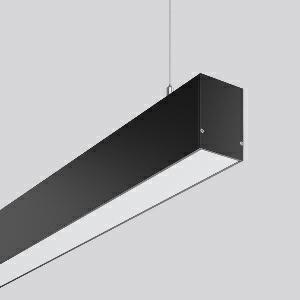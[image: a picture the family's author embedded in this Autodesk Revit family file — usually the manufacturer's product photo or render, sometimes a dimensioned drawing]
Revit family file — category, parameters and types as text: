
# Revit family: less_is_more_50_312313_003_1_1fba
name_source: partatom
category: Lighting Fixtures
units: mm (PartAtom-declared; Revit-internal decimal feet)

## family parameters
Cut with Voids When Loaded = No
Host = Face
Light Source = No
Part Type = Normal
Room Calculation Point = No
Round Connector Dimension = Use Diameter
Shared = No

## types (1)
- LESS IS MORE 50 (1 x LED Modul 840, 4050 lm, 4000)
    Apparent Load = 34 VA
    CIE Flux Codes = 48 79 95 100 100
    Color Rendering = 80
    Color Temperature = 4000
    Default Elevation = 1800 mm
    Description = Series: LESS IS MORE 50
Linear pendant luminaire for aesthetically sophisticated lighting. Housing: extruded aluminium profile, powder-coated. End cap aluminium powder-coated. Canopy made of aluminium, powder-coated. Diffuser made of non-yellowing plastic (PMMA), opal. Direct light emission. Suitable for pendant. 2-point steel cable suspension freely positionable and infinitely height-adjustable. Special lengths available on request. LED unit with integrated converter interchangeable and removable. Suitable for through-wiring. With sensors or as a safety luminaire on request. 
Colour: deep black, matt (RAL 9005)
Length: 1407 mm
Width: 57 mm
Height: 75 mm
Suspension length: 2000 mm
Lamp: LED
Socket: without socket
Colour temperature: 4000K
Colour rendering index (CRI): 80
System power: 34 W
Rated luminous flux: 4050 lm
Luminous efficiency: 119 lm/W
Control gear: Regulated power supply
Protection class: I
Type of protection: IP 20
    Height = 75 mm
    Lamp = 1 x LED Modul 840
    Lamp Light Flux = 4050 lm
    Lamp count = 1
    Length = 1407 mm
    Lifetime = 50000 h
    Luminous efficacy = 119 lm/W
    Manufacturer = RZB
    ModVariant = No
    Model = 312313.003.1
    Mounting Place = Ceiling
    Mounting Type = Pendant
    Number of Poles = 1
    OnlyDefault = Yes
    Power Factor = 1
    Product Name = LESS IS MORE 50
    Product group = Pendant LED linear luminaires
    ProductGroupID = 907
    Protection Class = Protection class I
    Protection Degree = IP 20
    RLX_Detail_Level = 1
    RLX_Emergency_Light_Flux = 0 lm
    RLX_Emergency_Type = 0
    RLX_Emergency_Type_DB = No
    RlxData = <blob elided: 28881 chars, md5=77074a79>
    Socket = socket
    Standby Power = 0 W
    System Light Flux = 4050 lm
    System Power = 34 W
    Type Comments = Product without accessories
    Type Image = 312318.003.jpg
    URL = http://relux.com
    VarID = ---
    Voltage = 230 V
    Voltage Range = 220-240 V
    Weight = 0.00 kg
    Width = 57 mm

## geometry (parser evidence)
native form markers: Blend x4, Sweep x9
no freeform markers — native parametric forms only
